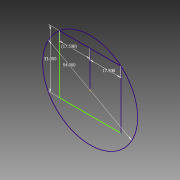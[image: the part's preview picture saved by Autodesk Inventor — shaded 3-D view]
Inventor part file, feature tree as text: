
AUTODESK INVENTOR PART (.ipt)
format: ipt  version: 2013 (Build 170138000, 138)  size: 65,024 bytes
history: native  units: in
note: dims shown in document units (in); Inventor stores cm internally (conversion verified against a paired STEP export)
features: sketch x1
ambient origin geometry x8: Origin, YZ Plane, XZ Plane, XY Plane, X Axis, Y Axis, Z Axis, Center Point
feature tree (1):
  sketch  "Sketch1"  dims[d0=54.0in d4=17.5in d5=17.5in d6=33.0in]
